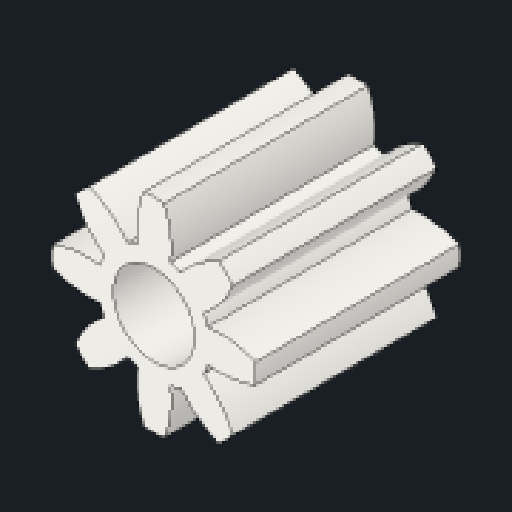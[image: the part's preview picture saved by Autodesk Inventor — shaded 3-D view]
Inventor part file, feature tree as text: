
AUTODESK INVENTOR PART (.ipt)
format: ipt  version: 2023.2 (Build 272271030, 271C)  size: 184,320 bytes
history: native  units: mm (DEFAULTED — no unit token found)
features: plane x3, other x3, sketch x3, extrude x1, hole x1
ambient origin geometry x8: Origin, YZ Plane, XZ Plane, XY Plane, X Axis, Y Axis, Z Axis, Center Point
bodies: Solid1 (feature_tree)
feature tree (11):
  extrude  "Extrusion1"  Depth=10.0mm TaperAngle=0.0deg
  plane  "Work Plane2"
  plane  "Work Plane8"
  plane  "Work Plane9"
  other  "Spur Gear"
  hole  "Hole1"  [1 undecoded]
  sketch  "Sketch1"  dims[d0=10.0mm d1=10.0mm d2=0.0mm]
  sketch  "Sketch2"  dims[d3=8.0mm d4=10.0mm d5=0.0mm]
  other  "Srf1"
  sketch  "Sketch3"  dims[d16=19.0mm d17=0.0mm d34=22.5deg d39=0.0mm d41=0.0mm d43=19.0mm d46=19.0mm d47=0.0mm d48=0.0mm d49=4.0mm d50=6.0mm d51=4.0mm d52=2.0mm d53=90.0deg d54=6.3mm d55=20.594885mm]
  other  "Pitch Diameter"
note: 1 required parameter value undecoded (feature->parameter linkage not recoverable at this tier; creation-order binding heuristic only, values carry confidence <= 0.55)
